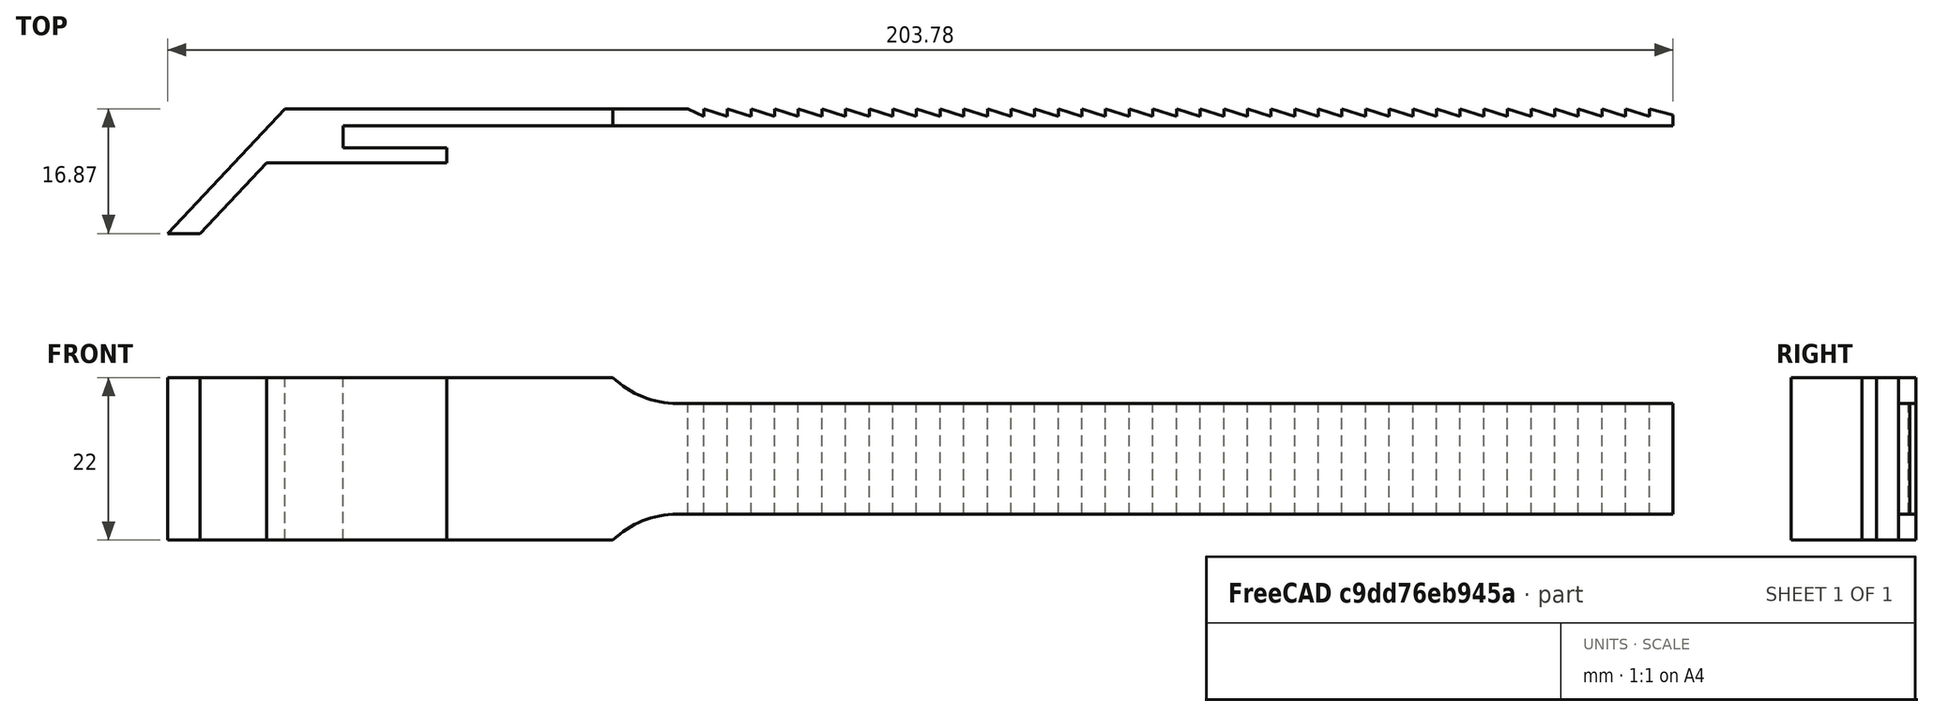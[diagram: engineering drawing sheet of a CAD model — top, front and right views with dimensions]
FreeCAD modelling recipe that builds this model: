
FCSTD DOCUMENT  (FreeCAD 0.19R24291 (Git))
Label: sangles
License: All rights reserved
LicenseURL: http://en.wikipedia.org/wiki/All_rights_reserved
objects: Sketcher::SketchObject×2, PartDesign::Pad×1, PartDesign::Pocket×1, PartDesign::Body×1
note: 7 computed .brp shape members not serialized (recipe doc carries the construction recipe); baked Part::Feature solids carry a one-line shape summary decoded from their .brp

FEATURE [Sketcher::SketchObject] Sketch
  FullyConstrained = false
  MapMode = 5
  Support = -> [XY_Plane]
  sketch-geometry (98):
    g0: LineSegment StartX=0.810902 StartY=9.5672 StartZ=0 EndX=25.1998 EndY=9.5672 EndZ=0
    g1: LineSegment StartX=25.1998 StartY=9.5672 StartZ=0 EndX=25.1998 EndY=11.5672 EndZ=0
    g2: LineSegment StartX=25.1998 StartY=11.5672 StartZ=0 EndX=11.1998 EndY=11.5672 EndZ=0
    g3: LineSegment StartX=11.1998 StartY=11.5672 StartZ=0 EndX=11.1998 EndY=14.5672 EndZ=0
    g4: LineSegment StartX=11.1998 StartY=14.5672 StartZ=0 EndX=191.2 EndY=14.5672 EndZ=0
    g5: LineSegment StartX=191.2 StartY=14.5672 StartZ=0 EndX=191.2 EndY=16.0672 EndZ=0
    g6: LineSegment StartX=59.9998 StartY=15.8672 StartZ=0 EndX=57.8322 EndY=16.8672 EndZ=0
    g7: LineSegment StartX=57.8322 StartY=16.8672 StartZ=0 EndX=3.31666 EndY=16.8672 EndZ=0
    g8: LineSegment StartX=0.810902 StartY=9.5672 StartZ=0 EndX=-8.20629 EndY=0.00158195 EndZ=0
    g9: LineSegment StartX=-8.20629 StartY=0.00158195 StartZ=0 EndX=-12.582 EndY=0.00158195 EndZ=0
    g10: LineSegment StartX=-12.582 StartY=0.00158195 StartZ=0 EndX=3.31666 EndY=16.8672 EndZ=0
    g11: LineSegment StartX=59.9998 StartY=15.8672 StartZ=0 EndX=59.9998 EndY=16.8672 EndZ=0
    g12: LineSegment StartX=59.9998 StartY=16.8672 StartZ=0 EndX=63.1998 EndY=15.8672 EndZ=0
    g13: LineSegment StartX=37.8701 StartY=15.8672 StartZ=0 EndX=90 EndY=15.8672 EndZ=0
    g14: LineSegment StartX=59.9998 StartY=15.8672 StartZ=0 EndX=63.1998 EndY=15.8657 EndZ=0
    g15: LineSegment StartX=63.1998 StartY=17.8488 StartZ=0 EndX=63.1998 EndY=15.4251 EndZ=0
    g16: LineSegment StartX=63.8826 StartY=16.8672 StartZ=0 EndX=59.1191 EndY=16.8672 EndZ=0
    g17: GeomPoint X=63.1998 Y=16.8672 Z=0
    g18: LineSegment StartX=63.1998 StartY=15.8672 StartZ=0 EndX=63.1998 EndY=16.8672 EndZ=0
    g19: LineSegment StartX=63.1998 StartY=16.8672 StartZ=0 EndX=66.3998 EndY=15.8672 EndZ=0
    g20: LineSegment StartX=66.3998 StartY=15.8672 StartZ=0 EndX=66.3998 EndY=16.8672 EndZ=0
    g21: LineSegment StartX=66.3998 StartY=16.8672 StartZ=0 EndX=69.5998 EndY=15.8672 EndZ=0
    g22: LineSegment StartX=69.5998 StartY=15.8672 StartZ=0 EndX=69.5998 EndY=16.8672 EndZ=0
    g23: LineSegment StartX=69.5998 StartY=16.8672 StartZ=0 EndX=72.7998 EndY=15.8672 EndZ=0
    g24: LineSegment StartX=72.7998 StartY=15.8672 StartZ=0 EndX=72.7998 EndY=16.8672 EndZ=0
    g25: LineSegment StartX=72.7998 StartY=16.8672 StartZ=0 EndX=75.9998 EndY=15.8672 EndZ=0
    g26: LineSegment StartX=75.9998 StartY=15.8672 StartZ=0 EndX=75.9998 EndY=16.8672 EndZ=0
    g27: LineSegment StartX=75.9998 StartY=16.8672 StartZ=0 EndX=79.1998 EndY=15.8672 EndZ=0
    g28: LineSegment StartX=79.1998 StartY=15.8672 StartZ=0 EndX=79.1998 EndY=16.8672 EndZ=0
    g29: LineSegment StartX=79.1998 StartY=16.8672 StartZ=0 EndX=82.3998 EndY=15.8672 EndZ=0
    g30: LineSegment StartX=82.3998 StartY=15.8672 StartZ=0 EndX=82.3998 EndY=16.8672 EndZ=0
    g31: LineSegment StartX=82.3998 StartY=16.8672 StartZ=0 EndX=85.5998 EndY=15.8672 EndZ=0
    g32: LineSegment StartX=85.5998 StartY=15.8672 StartZ=0 EndX=85.5998 EndY=16.8672 EndZ=0
    g33: LineSegment StartX=85.5998 StartY=16.8672 StartZ=0 EndX=88.7998 EndY=15.8672 EndZ=0
    g34: LineSegment StartX=88.7998 StartY=15.8672 StartZ=0 EndX=88.7998 EndY=16.8672 EndZ=0
    g35: LineSegment StartX=88.7998 StartY=16.8672 StartZ=0 EndX=91.9998 EndY=15.8672 EndZ=0
    g36: LineSegment StartX=91.9998 StartY=15.8672 StartZ=0 EndX=91.9998 EndY=16.8672 EndZ=0
    g37: LineSegment StartX=91.9998 StartY=16.8672 StartZ=0 EndX=95.1998 EndY=15.8672 EndZ=0
    g38: LineSegment StartX=95.1998 StartY=15.8672 StartZ=0 EndX=95.1998 EndY=16.8672 EndZ=0
    g39: LineSegment StartX=95.1998 StartY=16.8672 StartZ=0 EndX=98.3998 EndY=15.8672 EndZ=0
    g40: LineSegment StartX=98.3998 StartY=15.8672 StartZ=0 EndX=98.3998 EndY=16.8672 EndZ=0
    g41: LineSegment StartX=98.3998 StartY=16.8672 StartZ=0 EndX=101.6 EndY=15.8672 EndZ=0
    g42: LineSegment StartX=101.6 StartY=15.8672 StartZ=0 EndX=101.6 EndY=16.8672 EndZ=0
    g43: LineSegment StartX=101.6 StartY=16.8672 StartZ=0 EndX=104.8 EndY=15.8672 EndZ=0
    g44: LineSegment StartX=104.8 StartY=15.8672 StartZ=0 EndX=104.8 EndY=16.8672 EndZ=0
    g45: LineSegment StartX=104.8 StartY=16.8672 StartZ=0 EndX=108 EndY=15.8672 EndZ=0
    g46: LineSegment StartX=108 StartY=15.8672 StartZ=0 EndX=108 EndY=16.8672 EndZ=0
    g47: LineSegment StartX=108 StartY=16.8672 StartZ=0 EndX=111.2 EndY=15.8672 EndZ=0
    g48: LineSegment StartX=111.2 StartY=15.8672 StartZ=0 EndX=111.2 EndY=16.8672 EndZ=0
    g49: LineSegment StartX=111.2 StartY=16.8672 StartZ=0 EndX=114.4 EndY=15.8672 EndZ=0
    g50: LineSegment StartX=114.4 StartY=15.8672 StartZ=0 EndX=114.4 EndY=16.8672 EndZ=0
    g51: LineSegment StartX=114.4 StartY=16.8672 StartZ=0 EndX=117.6 EndY=15.8672 EndZ=0
    g52: LineSegment StartX=117.6 StartY=15.8672 StartZ=0 EndX=117.6 EndY=16.8672 EndZ=0
    g53: LineSegment StartX=117.6 StartY=16.8672 StartZ=0 EndX=120.8 EndY=15.8672 EndZ=0
    g54: LineSegment StartX=120.8 StartY=15.8672 StartZ=0 EndX=120.8 EndY=16.8672 EndZ=0
    g55: LineSegment StartX=120.8 StartY=16.8672 StartZ=0 EndX=124 EndY=15.8672 EndZ=0
    g56: LineSegment StartX=124 StartY=15.8672 StartZ=0 EndX=124 EndY=16.8672 EndZ=0
    g57: LineSegment StartX=124 StartY=16.8672 StartZ=0 EndX=127.2 EndY=15.8672 EndZ=0
    g58: LineSegment StartX=127.2 StartY=15.8672 StartZ=0 EndX=127.2 EndY=16.8672 EndZ=0
    g59: LineSegment StartX=127.2 StartY=16.8672 StartZ=0 EndX=130.4 EndY=15.8672 EndZ=0
    g60: LineSegment StartX=130.4 StartY=15.8672 StartZ=0 EndX=130.4 EndY=16.8672 EndZ=0
    g61: LineSegment StartX=130.4 StartY=16.8672 StartZ=0 EndX=133.6 EndY=15.8672 EndZ=0
    g62: LineSegment StartX=133.6 StartY=15.8672 StartZ=0 EndX=133.6 EndY=16.8672 EndZ=0
    g63: LineSegment StartX=133.6 StartY=16.8672 StartZ=0 EndX=136.8 EndY=15.8672 EndZ=0
    g64: LineSegment StartX=136.8 StartY=15.8672 StartZ=0 EndX=136.8 EndY=16.8672 EndZ=0
    g65: LineSegment StartX=136.8 StartY=16.8672 StartZ=0 EndX=140 EndY=15.8672 EndZ=0
    g66: LineSegment StartX=140 StartY=15.8672 StartZ=0 EndX=140 EndY=16.8672 EndZ=0
    g67: LineSegment StartX=140 StartY=16.8672 StartZ=0 EndX=143.2 EndY=15.8672 EndZ=0
    g68: LineSegment StartX=143.2 StartY=15.8672 StartZ=0 EndX=143.2 EndY=16.8672 EndZ=0
    g69: LineSegment StartX=143.2 StartY=16.8672 StartZ=0 EndX=146.4 EndY=15.8672 EndZ=0
    g70: LineSegment StartX=146.4 StartY=15.8672 StartZ=0 EndX=146.4 EndY=16.8672 EndZ=0
    g71: LineSegment StartX=146.4 StartY=16.8672 StartZ=0 EndX=149.6 EndY=15.8672 EndZ=0
    g72: LineSegment StartX=149.6 StartY=15.8672 StartZ=0 EndX=149.6 EndY=16.8672 EndZ=0
    g73: LineSegment StartX=149.6 StartY=16.8672 StartZ=0 EndX=152.8 EndY=15.8672 EndZ=0
    g74: LineSegment StartX=152.8 StartY=15.8672 StartZ=0 EndX=152.8 EndY=16.8672 EndZ=0
    g75: LineSegment StartX=152.8 StartY=16.8672 StartZ=0 EndX=156 EndY=15.8672 EndZ=0
    g76: LineSegment StartX=156 StartY=15.8672 StartZ=0 EndX=156 EndY=16.8672 EndZ=0
    g77: LineSegment StartX=156 StartY=16.8672 StartZ=0 EndX=159.2 EndY=15.8672 EndZ=0
    g78: LineSegment StartX=159.2 StartY=15.8672 StartZ=0 EndX=159.2 EndY=16.8672 EndZ=0
    g79: LineSegment StartX=159.2 StartY=16.8672 StartZ=0 EndX=162.4 EndY=15.8672 EndZ=0
    g80: LineSegment StartX=162.4 StartY=15.8672 StartZ=0 EndX=162.4 EndY=16.8672 EndZ=0
    g81: LineSegment StartX=162.4 StartY=16.8672 StartZ=0 EndX=165.6 EndY=15.8672 EndZ=0
    g82: LineSegment StartX=165.6 StartY=15.8672 StartZ=0 EndX=165.6 EndY=16.8672 EndZ=0
    g83: LineSegment StartX=165.6 StartY=16.8672 StartZ=0 EndX=168.8 EndY=15.8672 EndZ=0
    g84: LineSegment StartX=168.8 StartY=15.8672 StartZ=0 EndX=168.8 EndY=16.8672 EndZ=0
    g85: LineSegment StartX=168.8 StartY=16.8672 StartZ=0 EndX=172 EndY=15.8672 EndZ=0
    g86: LineSegment StartX=172 StartY=15.8672 StartZ=0 EndX=172 EndY=16.8672 EndZ=0
    g87: LineSegment StartX=172 StartY=16.8672 StartZ=0 EndX=175.2 EndY=15.8672 EndZ=0
    g88: LineSegment StartX=175.2 StartY=15.8672 StartZ=0 EndX=175.2 EndY=16.8672 EndZ=0
    g89: LineSegment StartX=175.2 StartY=16.8672 StartZ=0 EndX=178.4 EndY=15.8672 EndZ=0
    g90: LineSegment StartX=178.4 StartY=15.8672 StartZ=0 EndX=178.4 EndY=16.8672 EndZ=0
    g91: LineSegment StartX=178.4 StartY=16.8672 StartZ=0 EndX=181.6 EndY=15.8672 EndZ=0
    g92: LineSegment StartX=181.6 StartY=15.8672 StartZ=0 EndX=181.6 EndY=16.8672 EndZ=0
    g93: LineSegment StartX=181.6 StartY=16.8672 StartZ=0 EndX=184.8 EndY=15.8672 EndZ=0
    g94: LineSegment StartX=184.8 StartY=15.8672 StartZ=0 EndX=184.8 EndY=16.8672 EndZ=0
    g95: LineSegment StartX=184.8 StartY=16.8672 StartZ=0 EndX=188 EndY=15.8672 EndZ=0
    g96: LineSegment StartX=188 StartY=15.8672 StartZ=0 EndX=188 EndY=16.8672 EndZ=0
    g97: LineSegment StartX=188 StartY=16.8672 StartZ=0 EndX=191.2 EndY=16.0672 EndZ=0
  constraints (163):
    c: Horizontal(g0)
    c: Coincident(g0,g1)
    c: Vertical(g1)
    c: DistanceY(g1,g1) = 2
    c: Coincident(g1,g2)
    c: Horizontal(g2)
    c: Coincident(g3,g2)
    c: DistanceX(g2,g2) = 14
    c: Distance(g3) = 3
    c: Horizontal(g4)
    c: DistanceX(g4,g4) = 180
    c: Coincident(g3,g4)
    c: Coincident(g6,g7)
    c: Coincident(g5,g4)
    c: Vertical(g5)
    c: DistanceY(g6,g6) = 1
    c: Horizontal(g7)
    c: Coincident(g7,g10)
    c: Coincident(g8,g0)
    c: Parallel(g8,g10)
    c: Coincident(g8,g9)
    c: Coincident(g10,g9)
    c: Horizontal(g9)
    c: DistanceY(g2,g3) = 3
    c: Coincident(g11,g12)
    c: DistanceY(g11,g11) = 1
    c: Horizontal(g13)
    c: PointOnObject(g6,g13)
    c: PointOnObject(g12,g13)
    c: Vertical(g11)
    c: Coincident(g11,g6)
    c: Coincident(g11,g14)
    c: Distance(g14) = 3.2
    c: Angle(g14) = -0.000474528
    c: Vertical(g15)
    c: PointOnObject(g12,g15)
    c: Horizontal(g16)
    c: PointOnObject(g11,g16)
    c: PointOnObject(g17,g15)
    c: PointOnObject(g17,g16)
    c: Coincident(g18,g19)
    c: DistanceY(g18,g18) = 1
    c: Vertical(g18)
    c: Coincident(g20,g21)
    c: DistanceY(g20,g20) = 1
    c: Vertical(g20)
    c: Coincident(g22,g23)
    c: DistanceY(g22,g22) = 1
    c: Vertical(g22)
    c: Coincident(g24,g25)
    c: DistanceY(g24,g24) = 1
    c: Vertical(g24)
    c: Coincident(g26,g27)
    c: DistanceY(g26,g26) = 1
    c: Vertical(g26)
    c: Coincident(g28,g29)
    c: DistanceY(g28,g28) = 1
    c: Vertical(g28)
    c: Coincident(g30,g31)
    c: DistanceY(g30,g30) = 1
    c: Vertical(g30)
    c: Coincident(g32,g33)
    c: DistanceY(g32,g32) = 1
    c: Vertical(g32)
    c: Coincident(g34,g35)
    c: DistanceY(g34,g34) = 1
    c: Vertical(g34)
    c: Coincident(g36,g37)
    c: DistanceY(g36,g36) = 1
    c: Vertical(g36)
    c: Coincident(g38,g39)
    c: DistanceY(g38,g38) = 1
    c: Vertical(g38)
    c: Coincident(g40,g41)
    c: DistanceY(g40,g40) = 1
    c: Vertical(g40)
    c: Coincident(g42,g43)
    c: DistanceY(g42,g42) = 1
    c: Vertical(g42)
    c: Coincident(g44,g45)
    c: DistanceY(g44,g44) = 1
    c: Vertical(g44)
    c: Coincident(g46,g47)
    c: DistanceY(g46,g46) = 1
    c: Vertical(g46)
    c: Coincident(g48,g49)
    c: DistanceY(g48,g48) = 1
    c: Vertical(g48)
    c: Coincident(g50,g51)
    c: DistanceY(g50,g50) = 1
    c: Vertical(g50)
    c: Coincident(g52,g53)
    c: DistanceY(g52,g52) = 1
    c: Vertical(g52)
    c: Coincident(g54,g55)
    c: DistanceY(g54,g54) = 1
    c: Vertical(g54)
    c: Coincident(g56,g57)
    c: DistanceY(g56,g56) = 1
    c: Vertical(g56)
    c: Coincident(g58,g59)
    c: DistanceY(g58,g58) = 1
    c: Vertical(g58)
    c: Coincident(g60,g61)
    c: DistanceY(g60,g60) = 1
    c: Vertical(g60)
    c: Coincident(g62,g63)
    c: DistanceY(g62,g62) = 1
    c: Vertical(g62)
    c: Coincident(g64,g65)
    c: DistanceY(g64,g64) = 1
    c: Vertical(g64)
    c: Coincident(g66,g67)
    c: DistanceY(g66,g66) = 1
    c: Vertical(g66)
    c: Coincident(g68,g69)
    c: DistanceY(g68,g68) = 1
    c: Vertical(g68)
    c: Coincident(g70,g71)
    c: DistanceY(g70,g70) = 1
    c: Vertical(g70)
    c: Coincident(g72,g73)
    c: DistanceY(g72,g72) = 1
    c: Vertical(g72)
    c: Coincident(g74,g75)
    c: DistanceY(g74,g74) = 1
    c: Vertical(g74)
    c: Coincident(g76,g77)
    c: DistanceY(g76,g76) = 1
    c: Vertical(g76)
    c: Coincident(g78,g79)
    c: DistanceY(g78,g78) = 1
    c: Vertical(g78)
    c: Coincident(g80,g81)
    c: DistanceY(g80,g80) = 1
    c: Vertical(g80)
    c: Coincident(g82,g83)
    c: DistanceY(g82,g82) = 1
    c: Vertical(g82)
    c: Coincident(g84,g85)
    c: DistanceY(g84,g84) = 1
    c: Vertical(g84)
    c: Coincident(g86,g87)
    c: DistanceY(g86,g86) = 1
    c: Vertical(g86)
    c: Coincident(g88,g89)
    c: DistanceY(g88,g88) = 1
    c: Vertical(g88)
    c: Coincident(g90,g91)
    c: DistanceY(g90,g90) = 1
    c: Vertical(g90)
    c: Coincident(g92,g93)
    c: DistanceY(g92,g92) = 1
    c: Vertical(g92)
    c: Coincident(g94,g95)
    c: DistanceY(g94,g94) = 1
    c: Vertical(g94)
    c: Coincident(g96,g97)
    c: DistanceY(g96,g96) = 1
    c: Vertical(g96)
    c: Coincident(g5,g97)
    c: DistanceY(g5,g5) = 1.5
    c: DistanceY(g3,g7) = 2.3
FEATURE [PartDesign::Pad] Pad
  Direction = (1,1,1)
  Length = 22
  Length2 = 100
  Profile = -> Sketch
  Type = 0
FEATURE [Sketcher::SketchObject] Sketch001
  FullyConstrained = false
  MapMode = 5
  Placement = pos=(0,16.8672,0) rot=(0,0.707107,0.707107;3.14159rad)
  Support = -> [Pad]
  sketch-geometry (9):
    g0: LineSegment StartX=-230 StartY=11 StartZ=0 EndX=105.701 EndY=11 EndZ=0
    g1: ArcOfCircle CenterX=-197.533 CenterY=31.0405 CenterZ=0 NormalX=0 NormalY=0 NormalZ=1 AngleXU=0 Radius=12.5405 StartAngle=1.5708 EndAngle=4.71239
    g2: ArcOfCircle CenterX=-56.4043 CenterY=31.0405 CenterZ=0 NormalX=0 NormalY=0 NormalZ=1 AngleXU=0 Radius=12.5405 StartAngle=4.71239 EndAngle=7.85398
    g3: LineSegment StartX=-197.533 StartY=18.5 StartZ=0 EndX=-56.4043 EndY=18.5 EndZ=0
    g4: LineSegment StartX=-197.533 StartY=43.5809 StartZ=0 EndX=-56.4043 EndY=43.5809 EndZ=0
    g5: ArcOfCircle CenterX=-197.533 CenterY=-9.04047 CenterZ=0 NormalX=0 NormalY=0 NormalZ=1 AngleXU=0 Radius=12.5405 StartAngle=1.5708 EndAngle=4.71239
    g6: ArcOfCircle CenterX=-56.4043 CenterY=-9.04047 CenterZ=0 NormalX=0 NormalY=0 NormalZ=1 AngleXU=0 Radius=12.5405 StartAngle=4.71239 EndAngle=7.85398
    g7: LineSegment StartX=-197.533 StartY=3.5 StartZ=0 EndX=-56.4043 EndY=3.5 EndZ=0
    g8: LineSegment StartX=-197.533 StartY=-21.5809 StartZ=0 EndX=-56.4043 EndY=-21.5809 EndZ=0
  constraints (15):
    c: Horizontal(g0)
    c: DistanceY(g-1,g0) = 11
    c: Tangent(g1,g4) = 1.5708
    c: Tangent(g1,g3) = -1.5708
    c: Tangent(g3,g2) = -1.5708
    c: Tangent(g4,g2) = 1.5708
    c: Horizontal(g3)
    c: Equal(g1,g2)
    c: DistanceY(g0,g2) = 7.5
    c: Tangent(g5,g8) = -1.5708
    c: Tangent(g5,g7) = 1.5708
    c: Tangent(g7,g6) = 1.5708
    c: Tangent(g8,g6) = -1.5708
    c: Horizontal(g7)
    c: Equal(g5,g6)
FEATURE [PartDesign::Pocket] Pocket
  BaseFeature = -> Pad
  Length = 20
  Length2 = 100
  Profile = -> Sketch001
  Type = 0
FEATURE [PartDesign::Body] Body
  Group = -> [Sketch,Pad,Sketch001,Pocket]
  Origin = -> Origin
  Tip = -> Pocket
